# Revit family: Haworth_BuzziPleat_Ripple
name_source: partatom
category: Furniture
revit_build: Autodesk Revit 2018 (Build: 20170223_1515(x64)
units: mm (PartAtom-declared; Revit-internal decimal feet)

## family parameters
Cut with Voids When Loaded = No
Host = Face
Room Calculation Point = No
Shared = No

## types (2) — shared parameters
Assembly Code = E2020200
Manufacturer = Haworth
Max. Cable Length = 196.85 "
Min. Cable Length = 10 "
Model = HCBZ-PESS
Note = Verify Final Dim. w/ Haworth
Trim Finish = Haworth _ Paint _ Collection Black
URL = https://www.haworth.com
URL - Product = https://www.haworth.com
Warranty = https://www.haworth.com
zero-valued in all types: Default Elevation

## per-type parameters (varying)
| type | Actual Depth | Actual Height | Actual Width | Description | Large | Medium |
| HCBZ-PESS-RL - Large | 59.06 " | 7.68 " | 59.06 " | Haworth BuzziPleat Screen - Ripple - Large | Yes | No |
| HCBZ-PESS-RM - Medium | 39.37 " | 5.21 " | 39.37 " | Haworth BuzziPleat Screen - Ripple - Medium | No | Yes |

## geometry (parser evidence)
native form markers: Blend x4, Sweep x19
no freeform markers — native parametric forms only
